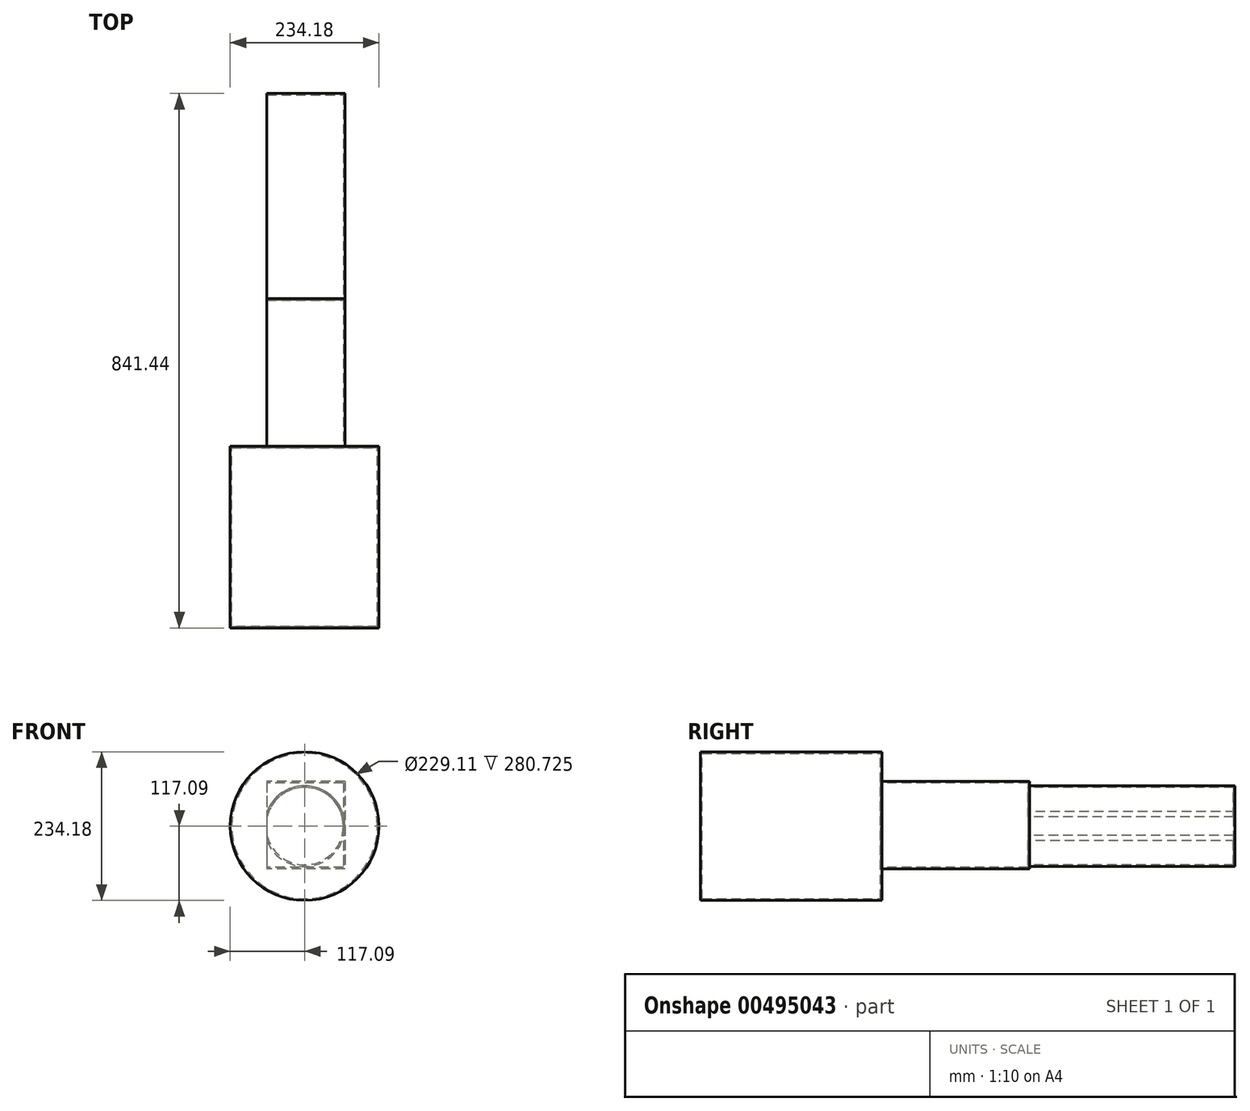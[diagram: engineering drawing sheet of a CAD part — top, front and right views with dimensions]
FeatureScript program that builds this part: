
annotation { "Feature Type Name" : "Feature", "Feature Type Description" : "" }
export const myFeature = defineFeature(function(context is Context, id is Id, definition is map)
    precondition{}
    {
        {
            var Q0;
            Q0=qCreatedBy(makeId("Front.planeOp"),FACE);
            var sketch = newSketch(context, id + "F0", { "sketchPlane" : qUnion([Q0])});
            skCircle(sketch, "E0", {"center": v(0, 0) * mm, "radius": 117.1 * mm});
            skSolve(sketch);
        }
        {
            var Q0;
            Q0=makeQuery(id+"F0.imprint","IMPRINT",FACE,{"disambiguationData":[TD([[makeQuery(id+"F0.imprint","IMPRINT",EDGE,{"derivedFrom":sQuery(id+"F0.wireOp",EDGE,"E0")}),1.0]])]});
            extrude(context, id + "F1", {"entities" : qUnion([Q0]), "depth" : 285.8 * mm});
        }
        {
            var Q0;
            Q0=makeQuery(id+"F1.opExtrude","CAP_FACE",FACE,{"disambiguationData":[OSD([sQuery(id+"F0.wireOp",EDGE,"E0")])],"isStart":true});
            var sketch = newSketch(context, id + "F2", { "sketchPlane" : qUnion([Q0])});
            skLineSegment(sketch, "E1.bottom", {"start": v(-63.57, 70.54) * mm, "end": v(59.3, 70.54) * mm});
            skLineSegment(sketch, "E1.top", {"start": v(-63.57, -67.05) * mm, "end": v(59.3, -67.05) * mm});
            skLineSegment(sketch, "E1.left", {"start": v(-63.57, 70.54) * mm, "end": v(-63.57, -67.05) * mm});
            skLineSegment(sketch, "E1.right", {"start": v(59.3, 70.54) * mm, "end": v(59.3, -67.05) * mm});
            skSolve(sketch);
        }
        {
            var Q0;
            Q0=makeQuery(id+"F2.imprint","IMPRINT",FACE,{"disambiguationData":[TD([[makeQuery(id+"F2.imprint","IMPRINT",EDGE,{"derivedFrom":sQuery(id+"F2.wireOp",EDGE,"E1.bottom")}),-1.0]])]});
            extrude(context, id + "F3", {"entities" : qUnion([Q0]), "operationType" : NewBodyOperationType.ADD, "depth" : 232.5 * mm});
        }
        {
            var Q0;
            Q0=makeQuery(id+"F3.opExtrude","CAP_FACE",FACE,{"disambiguationData":[OSD([sQuery(id+"F2.wireOp",EDGE,"E1.bottom"),sQuery(id+"F2.wireOp",EDGE,"E1.top"),sQuery(id+"F2.wireOp",EDGE,"E1.left"),sQuery(id+"F2.wireOp",EDGE,"E1.right")])],"isStart":false});
            var sketch = newSketch(context, id + "F4", { "sketchPlane" : qUnion([Q0])});
            skCircle(sketch, "E2", {"center": v(0, 0) * mm, "radius": 118.67 * mm});
            skSolve(sketch);
        }
        {
            var Q0;
            Q0=makeQuery(id+"F4.imprint","IMPRINT",FACE,{"disambiguationData":[TD([[makeQuery(id+"F4.imprint","IMPRINT",EDGE,{"derivedFrom":sQuery(id+"F4.wireOp",EDGE,"E2")}),1.0]])]});
            extrude(context, id + "F5", {"entities" : qUnion([Q0]), "depth" : 163 * mm});
        }
        {
            var Q0;
            Q0=makeQuery(id+"F5.opExtrude","SWEPT_BODY",BODY,{"disambiguationData":[OSD([sQuery(id+"F2.wireOp",EDGE,"E1.bottom"),sQuery(id+"F2.wireOp",EDGE,"E1.top"),sQuery(id+"F2.wireOp",EDGE,"E1.left"),sQuery(id+"F2.wireOp",EDGE,"E1.right"),sQuery(id+"F4.wireOp",EDGE,"E2")])]});
            deleteBodies(context, id + "F6", {"entities" : qUnion([Q0])});
        }
        {
            var Q0;
            Q0=makeQuery(id+"F3.opExtrude","CAP_FACE",FACE,{"disambiguationData":[OSD([sQuery(id+"F2.wireOp",EDGE,"E1.bottom"),sQuery(id+"F2.wireOp",EDGE,"E1.top"),sQuery(id+"F2.wireOp",EDGE,"E1.left"),sQuery(id+"F2.wireOp",EDGE,"E1.right")])],"isStart":false});
            var sketch = newSketch(context, id + "F7", { "sketchPlane" : qUnion([Q0])});
            skCircle(sketch, "E3", {"center": v(0, 0) * mm, "radius": 63.57 * mm});
            skSolve(sketch);
        }
        {
            var Q0;
            {var subQ0=sQuery(id+"F7.wireOp",EDGE,"E3");var subQ1=makeQuery(id+"F7.imprint","INTERSECT",VERTEX,{"derivedFrom":[makeQuery(id+"F3.opExtrude","CAP_EDGE",EDGE,{"disambiguationData":[OSD([sQuery(id+"F2.wireOp",EDGE,"E1.left")])],"isStart":false}),subQ0]});Q0=makeQuery(id+"F7.imprint","IMPRINT",FACE,{"disambiguationData":[TD([[makeQuery(id+"F7.imprint","IMPRINT",EDGE,{"disambiguationData":[TD([[subQ1,1.0]])],"derivedFrom":subQ0}),1.0]])]});}
            extrude(context, id + "F8", {"entities" : qUnion([Q0]), "operationType" : NewBodyOperationType.ADD, "depth" : 323.14 * mm});
        }
        {
            var Q0;
            {var subQ0=sQuery(id+"F2.wireOp",EDGE,"E1.right");Q0=makeQuery(id+"F8.boolean.opBoolean","MERGE",FACE,{"derivedFrom":[makeQuery(id+"F3.opExtrude","SWEPT_FACE",FACE,{"disambiguationData":[OSD([subQ0])]}),makeQuery(id+"F8.opExtrude","SWEPT_FACE",FACE,{"disambiguationData":[OSD([subQ0])]})]});}
            shell(context, id + "F9", {"entities" : qUnion([Q0]), "thickness" : 2.54 * mm});
        }
        {
            var Q0;
            Q0=makeQuery(id+"F8.opExtrude","CAP_FACE",FACE,{"disambiguationData":[OSD([sQuery(id+"F2.wireOp",EDGE,"E1.right"),sQuery(id+"F7.wireOp",EDGE,"E3")])],"isStart":false});
            var sketch = newSketch(context, id + "F10", { "sketchPlane" : qUnion([Q0])});
            skCircle(sketch, "E4", {"center": v(0, 0) * mm, "radius": 25.12 * mm});
            skSolve(sketch);
        }
        {
            var Q0;
            Q0=sQuery(id+"F10.wireOp",EDGE,"E4");
            extrude(context, id + "F11", {"bodyType" : ToolBodyType.SURFACE, "surfaceEntities" : qUnion([Q0]), "oppositeDirection" : true, "depth" : 2500.43 * mm});
        }
        {
            var Q0;
            Q0=makeQuery(id+"F1.opExtrude","CAP_EDGE",EDGE,{"disambiguationData":[OSD([sQuery(id+"F0.wireOp",EDGE,"E0")])],"isStart":false});
            var Q1;
            Q1=makeQuery(id+"F11.opExtrude","CAP_EDGE",EDGE,{"disambiguationData":[OSD([sQuery(id+"F10.wireOp",EDGE,"E4")])],"isStart":false});
            loft(context, id + "F12", {"bodyType" : ToolBodyType.SURFACE, "wireProfilesArray" : [{ "wireProfileEntities" : qUnion([Q0]) }, { "wireProfileEntities" : qUnion([Q1]) }]});
        }
    });
